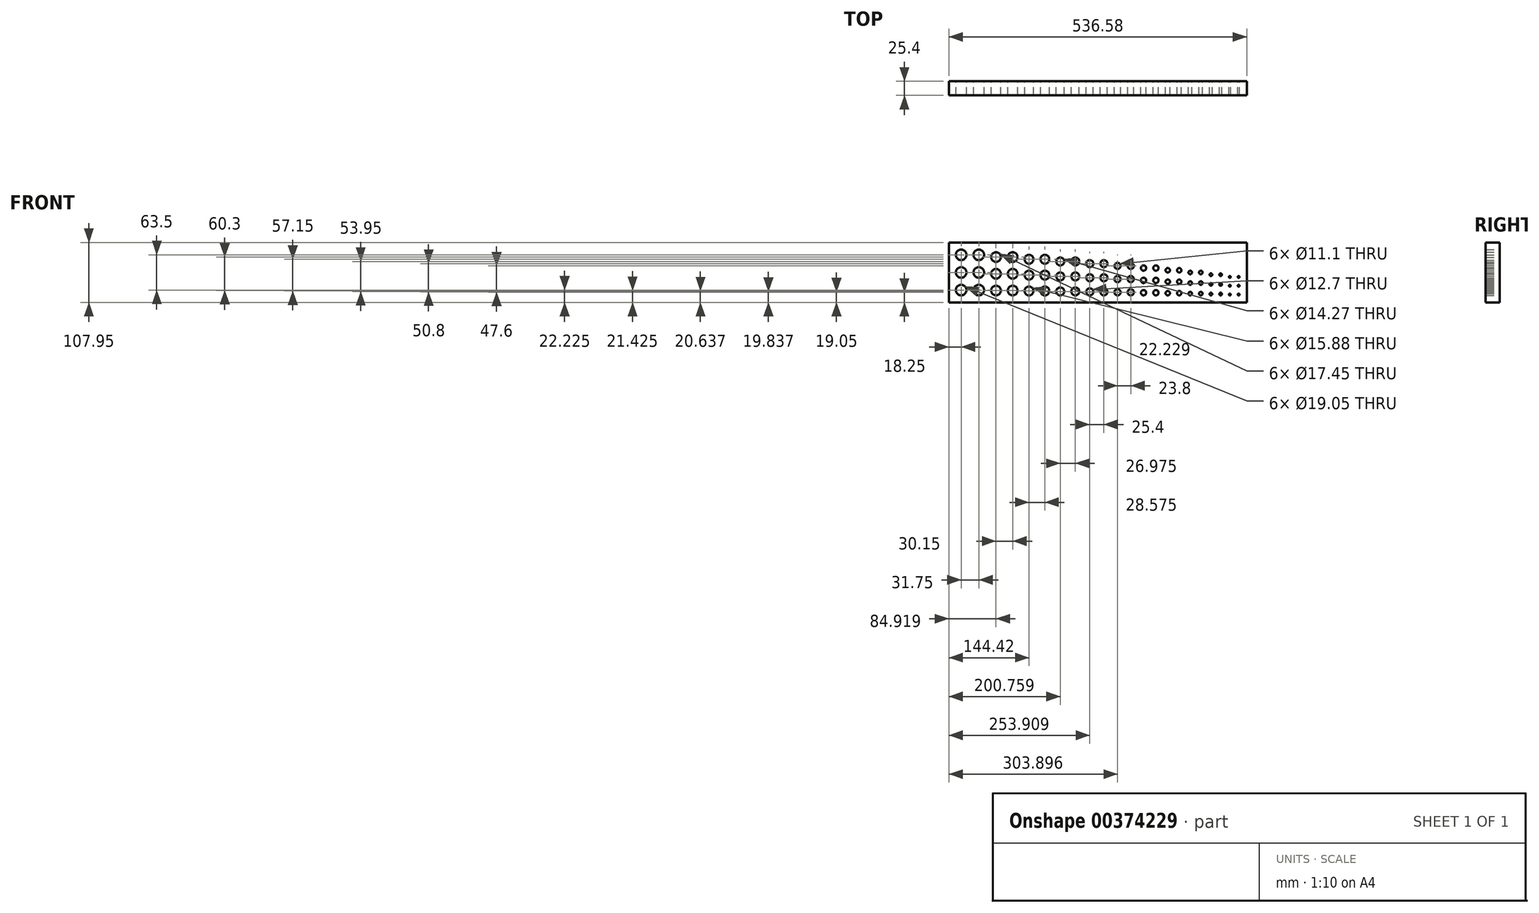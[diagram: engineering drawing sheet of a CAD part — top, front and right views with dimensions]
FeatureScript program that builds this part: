
annotation { "Feature Type Name" : "Feature", "Feature Type Description" : "" }
export const myFeature = defineFeature(function(context is Context, id is Id, definition is map)
    precondition{}
    {
        {
            var Q0;
            Q0=qCreatedBy(makeId("Front.planeOp"),FACE);
            var sketch = newSketch(context, id + "F0", { "sketchPlane" : qUnion([Q0])});
            skLineSegment(sketch, "E0.bottom", {"start": v(-230.09, 69.91) * mm, "end": v(306.49, 69.91) * mm});
            skLineSegment(sketch, "E0.top", {"start": v(-230.09, -38.04) * mm, "end": v(306.49, -38.04) * mm});
            skLineSegment(sketch, "E0.left", {"start": v(-230.09, 69.91) * mm, "end": v(-230.09, -38.04) * mm});
            skLineSegment(sketch, "E0.right", {"start": v(306.49, 69.91) * mm, "end": v(306.49, -38.04) * mm});
            skCircle(sketch, "E1", {"center": v(164.24, -21.38) * mm, "radius": 3.96 * mm});
            skCircle(sketch, "E2", {"center": v(120.6, -20.58) * mm, "radius": 4.76 * mm});
            skCircle(sketch, "E3", {"center": v(73.8, -19.8) * mm, "radius": 5.55 * mm});
            skCircle(sketch, "E4", {"center": v(23.82, -18.99) * mm, "radius": 6.35 * mm});
            skCircle(sketch, "E5", {"center": v(-29.33, -18.2) * mm, "radius": 7.14 * mm});
            skCircle(sketch, "E6", {"center": v(-85.67, -17.4) * mm, "radius": 7.94 * mm});
            skCircle(sketch, "E7", {"center": v(-145.17, -16.62) * mm, "radius": 8.72 * mm});
            skCircle(sketch, "E8", {"center": v(-207.86, -15.81) * mm, "radius": 9.53 * mm});
            skCircle(sketch, "E9.0.1.0", {"center": v(-207.86, 15.94) * mm, "radius": 9.53 * mm});
            skCircle(sketch, "E9.0.2.0", {"center": v(-207.86, 47.69) * mm, "radius": 9.53 * mm});
            skLineSegment(sketch, "E9.direction1", {"start": v(-207.86, -15.81) * mm, "end": v(-176.11, -15.81) * mm, "construction": true});
            skLineSegment(sketch, "E9.direction2", {"start": v(-207.86, -15.81) * mm, "end": v(-207.86, 15.94) * mm, "construction": true});
            skCircle(sketch, "E10.0.1.0", {"center": v(-176.11, -15.81) * mm, "radius": 9.53 * mm});
            skCircle(sketch, "E10.0.1.1", {"center": v(-176.11, 15.94) * mm, "radius": 9.53 * mm});
            skCircle(sketch, "E10.0.1.2", {"center": v(-176.11, 47.69) * mm, "radius": 9.53 * mm});
            skCircle(sketch, "E11.0.1.0", {"center": v(-145.17, 13.53) * mm, "radius": 8.72 * mm});
            skCircle(sketch, "E11.0.2.0", {"center": v(-145.17, 43.68) * mm, "radius": 8.72 * mm});
            skCircle(sketch, "E11.1.0.0", {"center": v(-115.02, -16.62) * mm, "radius": 8.72 * mm});
            skCircle(sketch, "E11.1.1.0", {"center": v(-115.02, 13.53) * mm, "radius": 8.72 * mm});
            skCircle(sketch, "E11.1.2.0", {"center": v(-115.02, 43.68) * mm, "radius": 8.72 * mm});
            skLineSegment(sketch, "E11.direction1", {"start": v(-145.17, -16.62) * mm, "end": v(-115.02, -16.62) * mm, "construction": true});
            skLineSegment(sketch, "E11.direction2", {"start": v(-145.17, -16.62) * mm, "end": v(-145.17, 13.53) * mm, "construction": true});
            skCircle(sketch, "E12.0.1.0", {"center": v(-85.67, 11.17) * mm, "radius": 7.94 * mm});
            skCircle(sketch, "E12.0.2.0", {"center": v(-85.67, 39.75) * mm, "radius": 7.94 * mm});
            skCircle(sketch, "E12.1.0.0", {"center": v(-57.1, -17.4) * mm, "radius": 7.94 * mm});
            skCircle(sketch, "E12.1.1.0", {"center": v(-57.1, 11.17) * mm, "radius": 7.94 * mm});
            skCircle(sketch, "E12.1.2.0", {"center": v(-57.1, 39.75) * mm, "radius": 7.94 * mm});
            skLineSegment(sketch, "E12.direction1", {"start": v(-85.67, -17.4) * mm, "end": v(-57.1, -17.4) * mm, "construction": true});
            skLineSegment(sketch, "E12.direction2", {"start": v(-85.67, -17.4) * mm, "end": v(-85.67, 11.17) * mm, "construction": true});
            skCircle(sketch, "E13.0.1.0", {"center": v(-29.33, 8.77) * mm, "radius": 7.14 * mm});
            skCircle(sketch, "E13.0.2.0", {"center": v(-29.33, 35.75) * mm, "radius": 7.14 * mm});
            skCircle(sketch, "E13.1.0.0", {"center": v(-2.36, -18.2) * mm, "radius": 7.14 * mm});
            skCircle(sketch, "E13.1.1.0", {"center": v(-2.36, 8.77) * mm, "radius": 7.14 * mm});
            skCircle(sketch, "E13.1.2.0", {"center": v(-2.36, 35.75) * mm, "radius": 7.14 * mm});
            skLineSegment(sketch, "E13.direction1", {"start": v(-29.33, -18.2) * mm, "end": v(-2.36, -18.2) * mm, "construction": true});
            skLineSegment(sketch, "E13.direction2", {"start": v(-29.33, -18.2) * mm, "end": v(-29.33, 8.77) * mm, "construction": true});
            skCircle(sketch, "E14.0.1.0", {"center": v(23.82, 6.41) * mm, "radius": 6.35 * mm});
            skCircle(sketch, "E14.0.2.0", {"center": v(23.82, 31.81) * mm, "radius": 6.35 * mm});
            skCircle(sketch, "E14.1.0.0", {"center": v(49.22, -18.99) * mm, "radius": 6.35 * mm});
            skCircle(sketch, "E14.1.1.0", {"center": v(49.22, 6.41) * mm, "radius": 6.35 * mm});
            skCircle(sketch, "E14.1.2.0", {"center": v(49.22, 31.81) * mm, "radius": 6.35 * mm});
            skLineSegment(sketch, "E14.direction1", {"start": v(23.82, -18.99) * mm, "end": v(49.22, -18.99) * mm, "construction": true});
            skLineSegment(sketch, "E14.direction2", {"start": v(23.82, -18.99) * mm, "end": v(23.82, 6.41) * mm, "construction": true});
            skCircle(sketch, "E15.0.1.0", {"center": v(73.8, 4) * mm, "radius": 5.55 * mm});
            skCircle(sketch, "E15.0.2.0", {"center": v(73.8, 27.8) * mm, "radius": 5.55 * mm});
            skCircle(sketch, "E15.1.0.0", {"center": v(97.6, -19.8) * mm, "radius": 5.55 * mm});
            skCircle(sketch, "E15.1.1.0", {"center": v(97.6, 4) * mm, "radius": 5.55 * mm});
            skCircle(sketch, "E15.1.2.0", {"center": v(97.6, 27.8) * mm, "radius": 5.55 * mm});
            skLineSegment(sketch, "E15.direction1", {"start": v(73.8, -19.8) * mm, "end": v(97.6, -19.8) * mm, "construction": true});
            skLineSegment(sketch, "E15.direction2", {"start": v(73.8, -19.8) * mm, "end": v(73.8, 4) * mm, "construction": true});
            skCircle(sketch, "E16.0.1.0", {"center": v(120.6, 1.65) * mm, "radius": 4.76 * mm});
            skCircle(sketch, "E16.0.2.0", {"center": v(120.6, 23.87) * mm, "radius": 4.76 * mm});
            skCircle(sketch, "E16.1.0.0", {"center": v(142.83, -20.58) * mm, "radius": 4.76 * mm});
            skCircle(sketch, "E16.1.1.0", {"center": v(142.83, 1.65) * mm, "radius": 4.76 * mm});
            skCircle(sketch, "E16.1.2.0", {"center": v(142.83, 23.87) * mm, "radius": 4.76 * mm});
            skLineSegment(sketch, "E16.direction1", {"start": v(120.6, -20.58) * mm, "end": v(142.83, -20.58) * mm, "construction": true});
            skLineSegment(sketch, "E16.direction2", {"start": v(120.6, -20.58) * mm, "end": v(120.6, 1.65) * mm, "construction": true});
            skCircle(sketch, "E17.0.1.0", {"center": v(164.24, -0.75) * mm, "radius": 3.96 * mm});
            skCircle(sketch, "E17.0.2.0", {"center": v(164.24, 19.87) * mm, "radius": 3.96 * mm});
            skCircle(sketch, "E17.1.0.0", {"center": v(184.86, -21.38) * mm, "radius": 3.96 * mm});
            skCircle(sketch, "E17.1.1.0", {"center": v(184.86, -0.75) * mm, "radius": 3.96 * mm});
            skCircle(sketch, "E17.1.2.0", {"center": v(184.86, 19.87) * mm, "radius": 3.96 * mm});
            skLineSegment(sketch, "E17.direction1", {"start": v(164.24, -21.38) * mm, "end": v(184.86, -21.38) * mm, "construction": true});
            skLineSegment(sketch, "E17.direction2", {"start": v(164.24, -21.38) * mm, "end": v(164.24, -0.75) * mm, "construction": true});
            skCircle(sketch, "E18", {"center": v(204.69, -22.16) * mm, "radius": 3.17 * mm});
            skCircle(sketch, "E19.0.1.0", {"center": v(204.69, -3.11) * mm, "radius": 3.17 * mm});
            skCircle(sketch, "E19.0.2.0", {"center": v(204.69, 15.94) * mm, "radius": 3.17 * mm});
            skCircle(sketch, "E19.1.0.0", {"center": v(223.74, -22.16) * mm, "radius": 3.17 * mm});
            skCircle(sketch, "E19.1.1.0", {"center": v(223.74, -3.11) * mm, "radius": 3.17 * mm});
            skCircle(sketch, "E19.1.2.0", {"center": v(223.74, 15.94) * mm, "radius": 3.17 * mm});
            skLineSegment(sketch, "E19.direction1", {"start": v(204.69, -22.16) * mm, "end": v(223.74, -22.16) * mm, "construction": true});
            skLineSegment(sketch, "E19.direction2", {"start": v(204.69, -22.16) * mm, "end": v(204.69, -3.11) * mm, "construction": true});
            skCircle(sketch, "E20", {"center": v(241.97, -22.97) * mm, "radius": 2.37 * mm});
            skCircle(sketch, "E21.0.1.0", {"center": v(241.97, -5.52) * mm, "radius": 2.37 * mm});
            skCircle(sketch, "E21.0.2.0", {"center": v(241.97, 11.93) * mm, "radius": 2.37 * mm});
            skCircle(sketch, "E21.1.0.0", {"center": v(259.42, -22.97) * mm, "radius": 2.37 * mm});
            skCircle(sketch, "E21.1.1.0", {"center": v(259.42, -5.52) * mm, "radius": 2.37 * mm});
            skCircle(sketch, "E21.1.2.0", {"center": v(259.42, 11.93) * mm, "radius": 2.37 * mm});
            skLineSegment(sketch, "E21.direction1", {"start": v(241.97, -22.97) * mm, "end": v(259.42, -22.97) * mm, "construction": true});
            skLineSegment(sketch, "E21.direction2", {"start": v(241.97, -22.97) * mm, "end": v(241.97, -5.52) * mm, "construction": true});
            skCircle(sketch, "E22", {"center": v(276.06, -23.75) * mm, "radius": 1.59 * mm});
            skCircle(sketch, "E23.0.1.0", {"center": v(276.06, -7.88) * mm, "radius": 1.59 * mm});
            skCircle(sketch, "E23.0.2.0", {"center": v(276.06, 8) * mm, "radius": 1.59 * mm});
            skCircle(sketch, "E23.1.0.0", {"center": v(291.94, -23.75) * mm, "radius": 1.59 * mm});
            skCircle(sketch, "E23.1.1.0", {"center": v(291.94, -7.88) * mm, "radius": 1.59 * mm});
            skCircle(sketch, "E23.1.2.0", {"center": v(291.94, 8) * mm, "radius": 1.59 * mm});
            skLineSegment(sketch, "E23.direction1", {"start": v(276.06, -23.75) * mm, "end": v(291.94, -23.75) * mm, "construction": true});
            skLineSegment(sketch, "E23.direction2", {"start": v(276.06, -23.75) * mm, "end": v(276.06, -7.88) * mm, "construction": true});
            skSolve(sketch);
        }
        {
            var Q0;
            Q0=makeQuery(id+"F0.imprint","IMPRINT",FACE,{"disambiguationData":[TD([[makeQuery(id+"F0.imprint","IMPRINT",EDGE,{"derivedFrom":sQuery(id+"F0.wireOp",EDGE,"E0.bottom")}),-1.0]])]});
            extrude(context, id + "F1", {"entities" : qUnion([Q0]), "depth" : 25.4 * mm});
        }
    });
